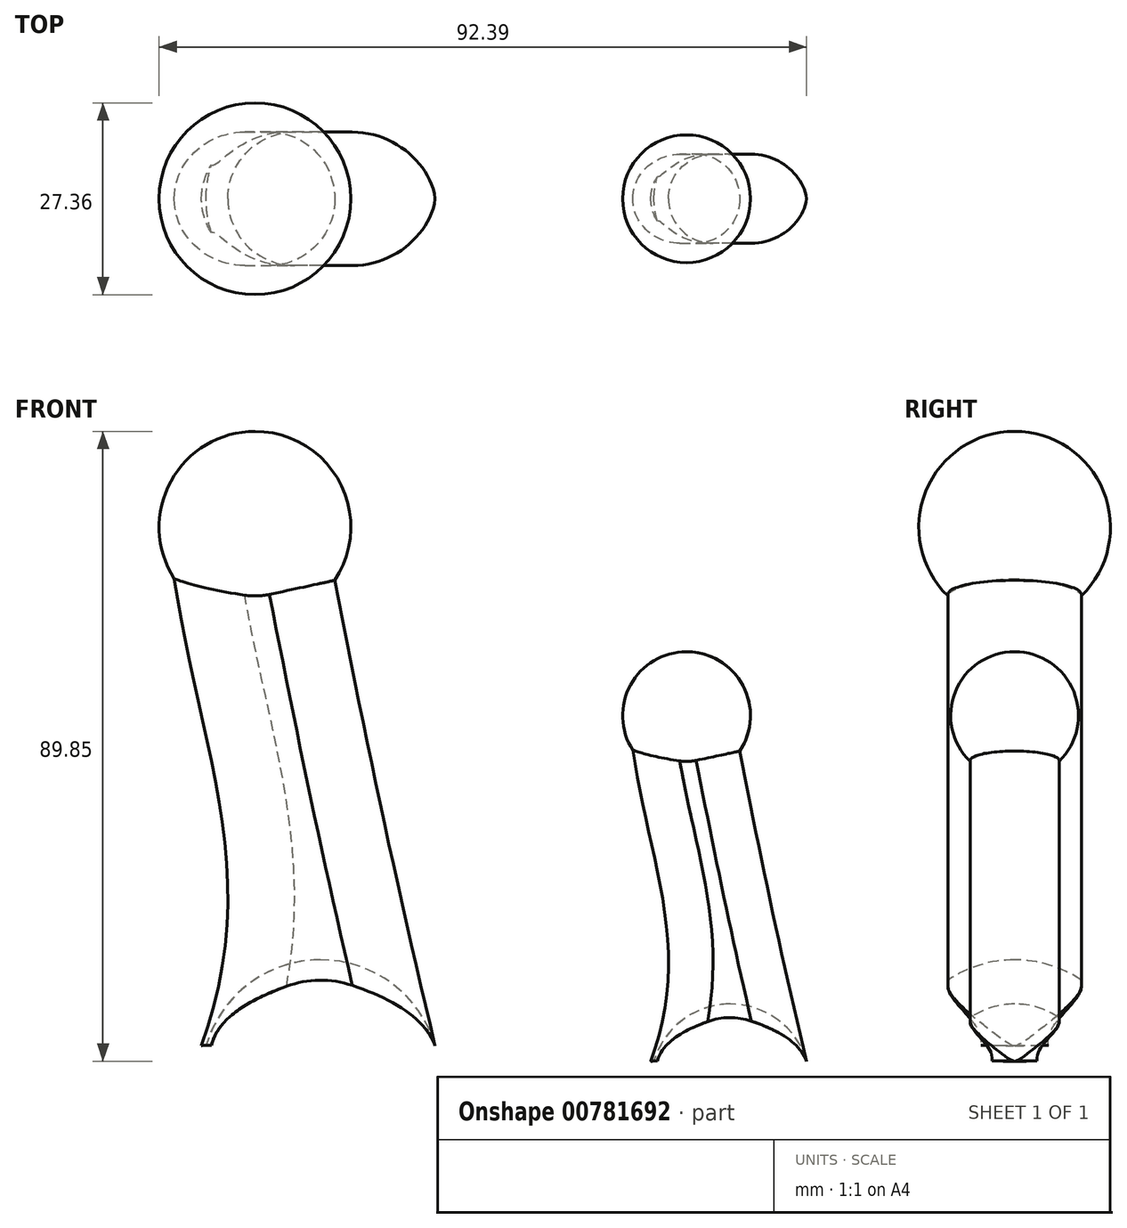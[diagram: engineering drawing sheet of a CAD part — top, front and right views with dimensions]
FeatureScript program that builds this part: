
annotation { "Feature Type Name" : "Feature", "Feature Type Description" : "" }
export const myFeature = defineFeature(function(context is Context, id is Id, definition is map)
    precondition{}
    {
        {
            var Q0;
            Q0=qCreatedBy(makeId("Front.planeOp"),FACE);
            var sketch = newSketch(context, id + "F0", { "sketchPlane" : qUnion([Q0])});
            skFitSpline(sketch, "E0", {"points": [v(21.55, 48.9) * mm, v(24.14, 4.46) * mm], "startDerivative": vector(8.19, -52.17) * mm, "endDerivative": vector(-17.38, -48.69) * mm});
            skFitSpline(sketch, "E1", {"points": [v(21.55, 48.9) * mm, v(36.79, 48.9) * mm], "startDerivative": vector(12.81, 0) * mm, "endDerivative": vector(12.81, 0) * mm});
            skFitSpline(sketch, "E2", {"points": [v(36.79, 48.9) * mm, v(46.37, 4.46) * mm], "startDerivative": vector(9.43, -48.17) * mm, "endDerivative": vector(11.32, -47.19) * mm});
            skFitSpline(sketch, "E3", {"points": [v(46.37, 4.46) * mm, v(24.14, 4.46) * mm], "startDerivative": vector(-22.82, 1.55) * mm, "endDerivative": vector(-27.53, -1.32) * mm});
            skPoint(sketch, "E4.second.point", {"position": v(36.79, 58.16) * mm});
            skSolve(sketch);
        }
        {
            var Q0;
            Q0 = qSketchRegion(id + "F0", true);
            extrude(context, id + "F1", {"entities" : qUnion([Q0]), "endBound" : BoundingType.SYMMETRIC, "depth" : 12.7 * mm, "offsetDistance" : 25.4 * mm});
        }
        {
            var Q0;
            Q0=makeQuery(id+"F1.opExtrude","CAP_EDGE",EDGE,{"disambiguationData":[OSD([sQuery(id+"F0.wireOp",EDGE,"E2")])],"isStart":false});
            var Q1;
            Q1=makeQuery(id+"F1.opExtrude","CAP_EDGE",EDGE,{"disambiguationData":[OSD([sQuery(id+"F0.wireOp",EDGE,"E0")])],"isStart":false});
            var Q2;
            Q2=makeQuery(id+"F1.opExtrude","CAP_EDGE",EDGE,{"disambiguationData":[OSD([sQuery(id+"F0.wireOp",EDGE,"E2")])],"isStart":true});
            var Q3;
            Q3=makeQuery(id+"F1.opExtrude","CAP_EDGE",EDGE,{"disambiguationData":[OSD([sQuery(id+"F0.wireOp",EDGE,"E0")])],"isStart":true});
            fillet(context, id + "F2", {"entities" : qUnion([Q0, Q1, Q2, Q3]), "radius" : 6.35 * mm, "tangentPropagation" : true, "allowEdgeOverflow" : false});
        }
        {
            var Q0;
            Q0=qCreatedBy(makeId("Front.planeOp"),FACE);
            var sketch = newSketch(context, id + "F3", { "sketchPlane" : qUnion([Q0])});
            skCircle(sketch, "E5", {"center": v(29.24, 53.76) * mm, "radius": 9.12 * mm});
            skLineSegment(sketch, "E6", {"start": v(29.24, 62.88) * mm, "end": v(29.24, 44.64) * mm});
            skSolve(sketch);
        }
        {
            var Q0;
            {var subQ0=sQuery(id+"F3.wireOp",EDGE,"E6");Q0=makeQuery(id+"F3.imprint","IMPRINT",FACE,{"disambiguationData":[TD([[makeQuery(id+"F3.imprint","IMPRINT",EDGE,{"derivedFrom":subQ0}),1.0]])]});}
            var Q1;
            Q1=sQuery(id+"F3.wireOp",EDGE,"E6");
            revolve(context, id + "F4", {"operationType" : NewBodyOperationType.ADD, "surfaceOperationType" : NewSurfaceOperationType.NEW, "entities" : qUnion([Q0]), "axis" : qUnion([Q1]), "revolveType" : RevolveType.FULL});
        }
        {
            var Q0;
            Q0=qCreatedBy(makeId("Front.planeOp"),FACE);
            var sketch = newSketch(context, id + "F5", { "sketchPlane" : qUnion([Q0])});
            skCircle(sketch, "E7", {"center": v(35.48, 1.27) * mm, "radius": 11.35 * mm});
            skPoint(sketch, "E7.first.point", {"position": v(24.62, 4.58) * mm});
            skPoint(sketch, "E7.second.point", {"position": v(46.32, 4.6) * mm});
            skPoint(sketch, "E7.third.point", {"position": v(39.22, -9.45) * mm});
            skLineSegment(sketch, "E8", {"start": v(35.48, 12.62) * mm, "end": v(35.48, -10.08) * mm});
            skSolve(sketch);
        }
        {
            var Q0;
            {var subQ0=sQuery(id+"F5.wireOp",EDGE,"E8");Q0=makeQuery(id+"F5.imprint","IMPRINT",FACE,{"disambiguationData":[TD([[makeQuery(id+"F5.imprint","IMPRINT",EDGE,{"derivedFrom":subQ0}),1.0]])]});}
            var Q1;
            Q1=sQuery(id+"F5.wireOp",EDGE,"E8");
            revolve(context, id + "F6", {"operationType" : NewBodyOperationType.REMOVE, "surfaceOperationType" : NewSurfaceOperationType.NEW, "entities" : qUnion([Q0]), "axis" : qUnion([Q1]), "revolveType" : RevolveType.FULL, "oppositeDirection" : true});
        }
        {
            var Q0;
            Q0=makeQuery(id+"F1.opExtrude","SWEPT_BODY",BODY,{"disambiguationData":[OSD([sQuery(id+"F0.wireOp",EDGE,"E0"),sQuery(id+"F0.wireOp",EDGE,"E1"),sQuery(id+"F0.wireOp",EDGE,"E2"),sQuery(id+"F0.wireOp",EDGE,"E3")])]});
            transform(context, id + "F7", {"entities" : qUnion([Q0]), "transformType" : TransformType.TRANSLATION_3D, "dx" : 0 * mm, "dy" : 0 * mm, "dz" : 0 * mm, "makeCopy" : true});
        }
        {
            var Q0;
            Q0=makeQuery(id+"F7.opPattern","COPY",BODY,{"derivedFrom":makeQuery(id+"F1.opExtrude","SWEPT_BODY",BODY,{"disambiguationData":[OSD([sQuery(id+"F0.wireOp",EDGE,"E0"),sQuery(id+"F0.wireOp",EDGE,"E1"),sQuery(id+"F0.wireOp",EDGE,"E2"),sQuery(id+"F0.wireOp",EDGE,"E3")])]}),"instanceName":"1"});
            deleteBodies(context, id + "F8", {"entities" : qUnion([Q0])});
        }
        {
            var Q0;
            Q0=makeQuery(id+"F1.opExtrude","SWEPT_BODY",BODY,{"disambiguationData":[OSD([sQuery(id+"F0.wireOp",EDGE,"E0"),sQuery(id+"F0.wireOp",EDGE,"E1"),sQuery(id+"F0.wireOp",EDGE,"E2"),sQuery(id+"F0.wireOp",EDGE,"E3")])]});
            transform(context, id + "F9", {"entities" : qUnion([Q0]), "transformType" : TransformType.TRANSLATION_3D, "dx" : -50.8 * mm, "dy" : 0 * mm, "dz" : 0 * mm, "makeCopy" : true});
        }
        {
            var Q0;
            Q0=makeQuery(id+"F9.opPattern","COPY",BODY,{"derivedFrom":makeQuery(id+"F1.opExtrude","SWEPT_BODY",BODY,{"disambiguationData":[OSD([sQuery(id+"F0.wireOp",EDGE,"E0"),sQuery(id+"F0.wireOp",EDGE,"E1"),sQuery(id+"F0.wireOp",EDGE,"E2"),sQuery(id+"F0.wireOp",EDGE,"E3")])]}),"instanceName":"1"});
            var Q1;
            Q1=qCreatedBy(makeId("Origin.pointOp"),VERTEX);
            transform(context, id + "F10", {"entities" : qUnion([Q0]), "transformType" : TransformType.SCALE_UNIFORMLY, "scale" : 1.5, "scalePoint" : qUnion([Q1]), "makeCopy" : false});
        }
    });
